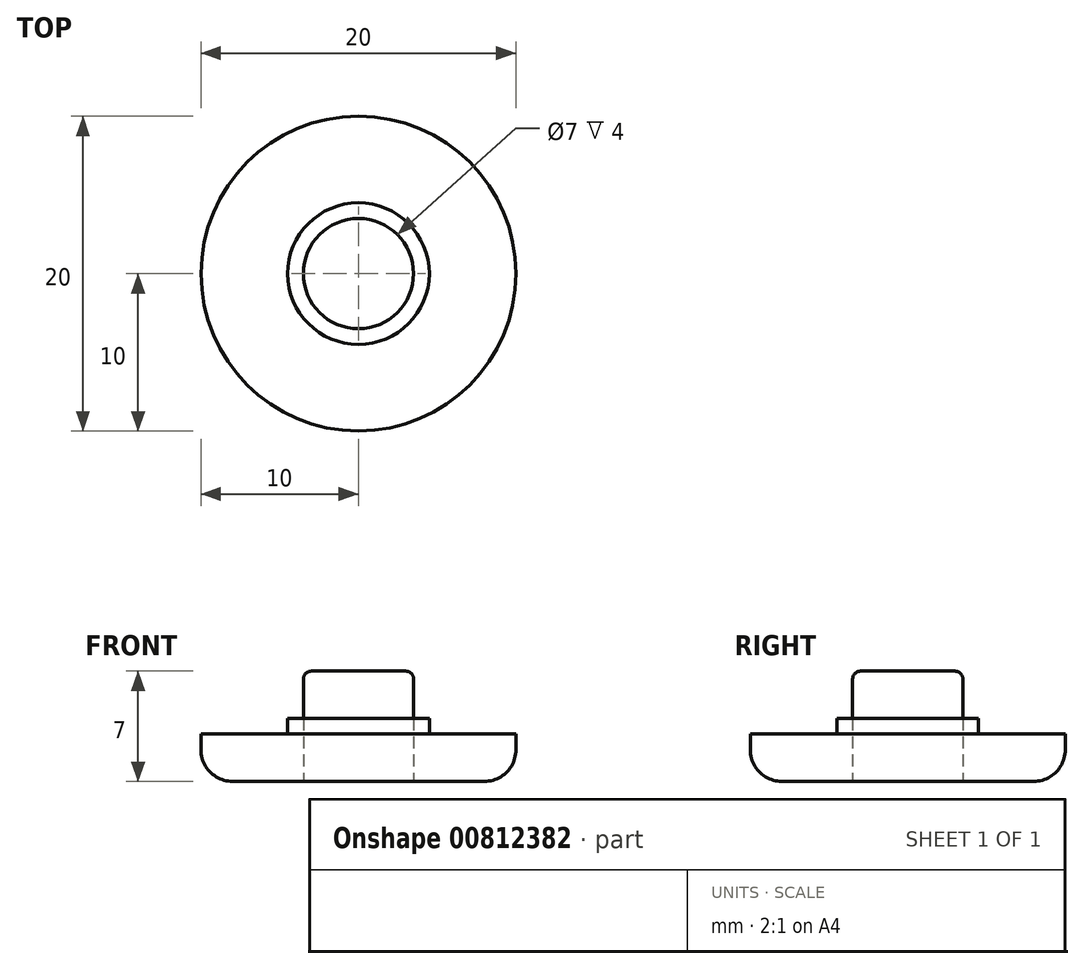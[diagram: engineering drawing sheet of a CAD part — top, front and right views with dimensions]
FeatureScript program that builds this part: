
annotation { "Feature Type Name" : "Feature", "Feature Type Description" : "" }
export const myFeature = defineFeature(function(context is Context, id is Id, definition is map)
    precondition{}
    {
        {
            var Q0;
            Q0=qCreatedBy(makeId("Top.planeOp"),FACE);
            var sketch = newSketch(context, id + "F0", { "sketchPlane" : qUnion([Q0])});
            skCircle(sketch, "E0", {"center": v(0, 0) * mm, "radius": 10 * mm});
            skCircle(sketch, "E1", {"center": v(0, 0) * mm, "radius": 4.5 * mm});
            skCircle(sketch, "E2", {"center": v(0, 0) * mm, "radius": 3.5 * mm});
            skSolve(sketch);
        }
        {
            var Q0;
            Q0=makeQuery(id+"F0.imprint","IMPRINT",FACE,{"disambiguationData":[TD([[makeQuery(id+"F0.imprint","IMPRINT",EDGE,{"derivedFrom":sQuery(id+"F0.wireOp",EDGE,"E2")}),1.0]])]});
            extrude(context, id + "F1", {"entities" : qUnion([Q0]), "depth" : 7 * mm, "offsetDistance" : 25 * mm});
        }
        {
            var Q0;
            Q0=makeQuery(id+"F0.imprint","IMPRINT",FACE,{"disambiguationData":[TD([[makeQuery(id+"F0.imprint","IMPRINT",EDGE,{"derivedFrom":sQuery(id+"F0.wireOp",EDGE,"E1")}),1.0]])]});
            extrude(context, id + "F2", {"entities" : qUnion([Q0]), "depth" : 4 * mm, "offsetDistance" : 25 * mm});
        }
        {
            var Q0;
            Q0=makeQuery(id+"F0.imprint","IMPRINT",FACE,{"disambiguationData":[TD([[makeQuery(id+"F0.imprint","IMPRINT",EDGE,{"derivedFrom":sQuery(id+"F0.wireOp",EDGE,"E0")}),1.0]])]});
            extrude(context, id + "F3", {"entities" : qUnion([Q0]), "operationType" : NewBodyOperationType.ADD, "depth" : 3 * mm, "offsetDistance" : 25 * mm});
        }
        {
            var Q0;
            Q0=makeQuery(id+"F3.opExtrude","CAP_EDGE",EDGE,{"disambiguationData":[OSD([sQuery(id+"F0.wireOp",EDGE,"E0")])],"isStart":true});
            fillet(context, id + "F4", {"entities" : qUnion([Q0]), "radius" : 2 * mm, "tangentPropagation" : true, "allowEdgeOverflow" : false});
        }
        {
            var Q0;
            Q0=makeQuery(id+"F1.opExtrude","CAP_FACE",FACE,{"disambiguationData":[OSD([sQuery(id+"F0.wireOp",EDGE,"E2")])],"isStart":false});
            fillet(context, id + "F5", {"entities" : qUnion([Q0]), "radius" : 0.5 * mm, "tangentPropagation" : true, "allowEdgeOverflow" : false});
        }
    });
